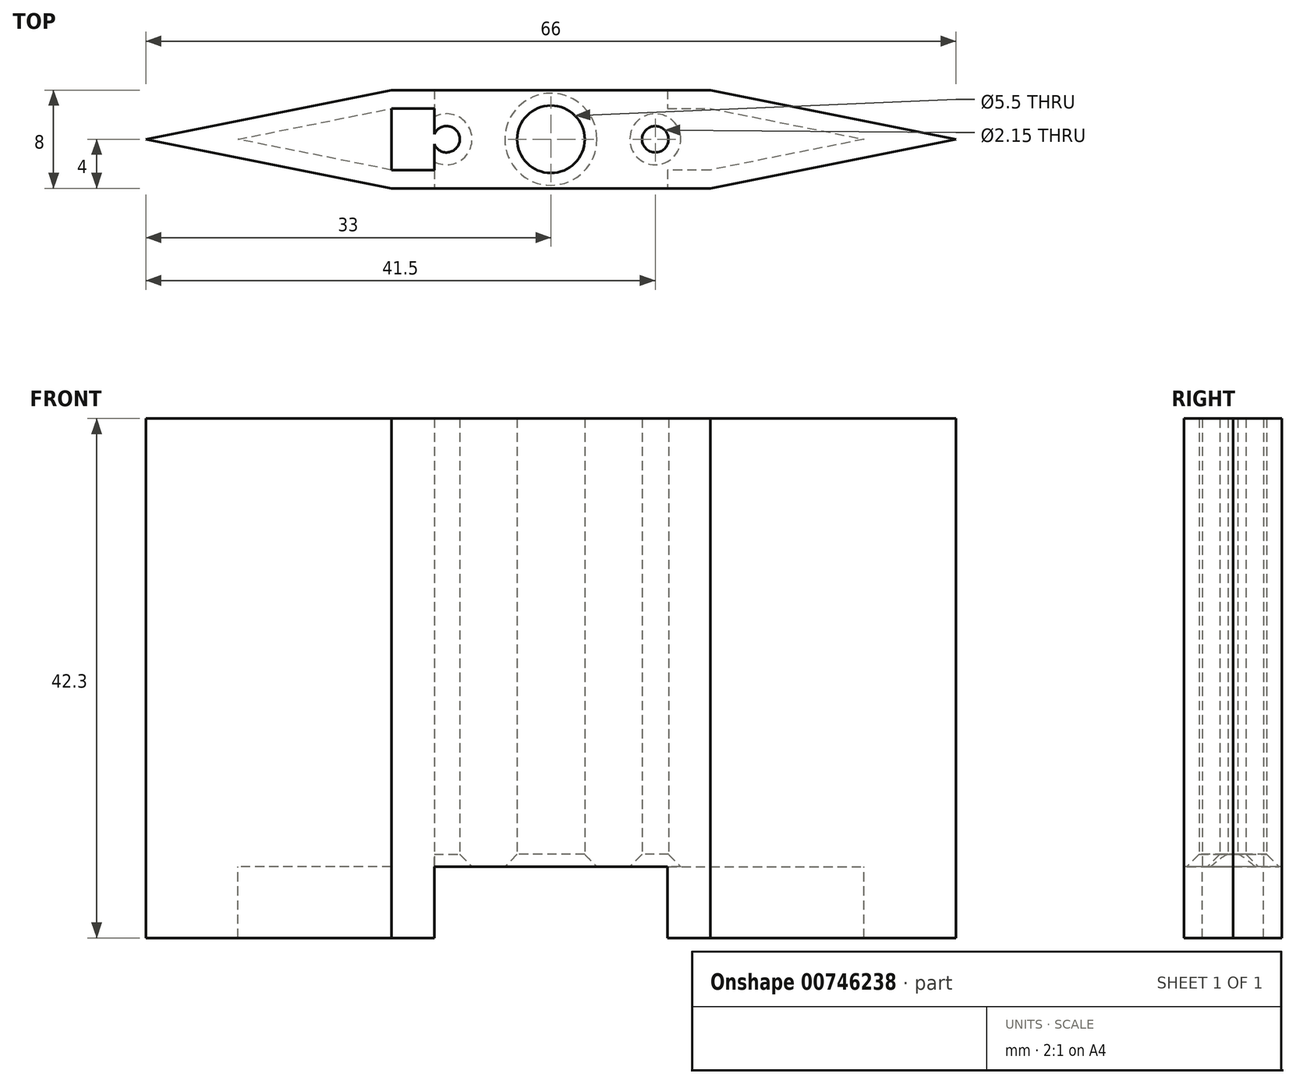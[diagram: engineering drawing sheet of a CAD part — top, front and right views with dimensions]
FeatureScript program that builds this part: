
annotation { "Feature Type Name" : "Feature", "Feature Type Description" : "" }
export const myFeature = defineFeature(function(context is Context, id is Id, definition is map)
    precondition{}
    {
        {
            var Q0;
            Q0=qCreatedBy(makeId("Top.planeOp"),FACE);
            var sketch = newSketch(context, id + "F0", { "sketchPlane" : qUnion([Q0])});
            skCircle(sketch, "E0", {"center": v(-8.5, 0) * mm, "radius": 1.07 * mm});
            skCircle(sketch, "E1", {"center": v(8.5, 0) * mm, "radius": 1.07 * mm});
            skLineSegment(sketch, "E2", {"start": v(-8.5, 0) * mm, "end": v(8.5, 0) * mm});
            skPoint(sketch, "E3", {"position": v(0, 0) * mm});
            skLineSegment(sketch, "E4", {"start": v(-33, 0) * mm, "end": v(-13, 4) * mm});
            skLineSegment(sketch, "E5", {"start": v(-13, 4) * mm, "end": v(13, 4) * mm});
            skLineSegment(sketch, "E6", {"start": v(13, 4) * mm, "end": v(33, 0) * mm});
            skLineSegment(sketch, "E7", {"start": v(33, 0) * mm, "end": v(13, -4) * mm});
            skLineSegment(sketch, "E8", {"start": v(13, -4) * mm, "end": v(-13, -4) * mm});
            skLineSegment(sketch, "E9", {"start": v(-13, -4) * mm, "end": v(-33, 0) * mm});
            skLineSegment(sketch, "E10", {"start": v(-13, 4) * mm, "end": v(-13, -4) * mm});
            skLineSegment(sketch, "E11", {"start": v(13, 4) * mm, "end": v(13, -4) * mm});
            skPoint(sketch, "E12", {"position": v(0, 4) * mm});
            skPoint(sketch, "E13", {"position": v(-13, 0) * mm});
            skLineSegment(sketch, "E14", {"start": v(-33, 0) * mm, "end": v(-13, 0) * mm});
            skLineSegment(sketch, "E15", {"start": v(13, 0) * mm, "end": v(33, 0) * mm});
            skCircle(sketch, "E16", {"center": v(0, 0) * mm, "radius": 2.75 * mm});
            skLineSegment(sketch, "E17", {"start": v(-13, 2.5) * mm, "end": v(13, 2.5) * mm});
            skLineSegment(sketch, "E18", {"start": v(13, 2.5) * mm, "end": v(25.5, 0) * mm});
            skLineSegment(sketch, "E19", {"start": v(25.5, 0) * mm, "end": v(13, -2.5) * mm});
            skLineSegment(sketch, "E20", {"start": v(13, -2.5) * mm, "end": v(-13, -2.5) * mm});
            skLineSegment(sketch, "E21", {"start": v(-13, -2.5) * mm, "end": v(-25.5, 0) * mm});
            skLineSegment(sketch, "E22", {"start": v(-25.5, 0) * mm, "end": v(-13, 2.5) * mm});
            skLineSegment(sketch, "E23", {"start": v(-9.5, 4) * mm, "end": v(-9.5, -4) * mm});
            skLineSegment(sketch, "E24", {"start": v(9.5, 4) * mm, "end": v(9.5, -4) * mm});
            skPoint(sketch, "E25", {"position": v(0, 12.17) * mm});
            skSolve(sketch);
        }
        {
            var Q0;
            Q0=makeQuery(id+"F0.imprint","IMPRINT",FACE,{"disambiguationData":[TD([[makeQuery(id+"F0.imprint","IMPRINT",EDGE,{"derivedFrom":sQuery(id+"F0.wireOp",EDGE,"E0")}),-1.0]])]});
            var Q1;
            {var subQ0=sQuery(id+"F0.wireOp",EDGE,"E9");Q1=makeQuery(id+"F0.imprint","IMPRINT",FACE,{"disambiguationData":[TD([[makeQuery(id+"F0.imprint","IMPRINT",EDGE,{"derivedFrom":subQ0}),-1.0]])]});}
            var Q2;
            {var subQ0=sQuery(id+"F0.wireOp",EDGE,"E4");Q2=makeQuery(id+"F0.imprint","IMPRINT",FACE,{"disambiguationData":[TD([[makeQuery(id+"F0.imprint","IMPRINT",EDGE,{"derivedFrom":subQ0}),-1.0]])]});}
            var Q3;
            {var subQ0=sQuery(id+"F0.wireOp",EDGE,"E7");Q3=makeQuery(id+"F0.imprint","IMPRINT",FACE,{"disambiguationData":[TD([[makeQuery(id+"F0.imprint","IMPRINT",EDGE,{"derivedFrom":subQ0}),-1.0]])]});}
            var Q4;
            {var subQ0=sQuery(id+"F0.wireOp",EDGE,"E6");Q4=makeQuery(id+"F0.imprint","IMPRINT",FACE,{"disambiguationData":[TD([[makeQuery(id+"F0.imprint","IMPRINT",EDGE,{"derivedFrom":subQ0}),-1.0]])]});}
            var Q5;
            {var subQ3=sQuery(id+"F0.wireOp",EDGE,"E21");Q5=makeQuery(id+"F0.imprint","IMPRINT",FACE,{"disambiguationData":[TD([[makeQuery(id+"F0.imprint","IMPRINT",EDGE,{"derivedFrom":subQ3}),-1.0]])]});}
            var Q6;
            {var subQ3=sQuery(id+"F0.wireOp",EDGE,"E22");Q6=makeQuery(id+"F0.imprint","IMPRINT",FACE,{"disambiguationData":[TD([[makeQuery(id+"F0.imprint","IMPRINT",EDGE,{"derivedFrom":subQ3}),-1.0]])]});}
            var Q7;
            {var subQ0=sQuery(id+"F0.wireOp",EDGE,"E5");Q7=makeQuery(id+"F0.imprint","IMPRINT",FACE,{"disambiguationData":[TD([[makeQuery(id+"F0.imprint","IMPRINT",EDGE,{"derivedFrom":subQ0}),-1.0]])]});}
            var Q8;
            {var subQ0=sQuery(id+"F0.wireOp",EDGE,"E8");Q8=makeQuery(id+"F0.imprint","IMPRINT",FACE,{"disambiguationData":[TD([[makeQuery(id+"F0.imprint","IMPRINT",EDGE,{"derivedFrom":subQ0}),-1.0]])]});}
            var Q9;
            {var subQ3=sQuery(id+"F0.wireOp",EDGE,"E19");Q9=makeQuery(id+"F0.imprint","IMPRINT",FACE,{"disambiguationData":[TD([[makeQuery(id+"F0.imprint","IMPRINT",EDGE,{"derivedFrom":subQ3}),-1.0]])]});}
            var Q10;
            {var subQ3=sQuery(id+"F0.wireOp",EDGE,"E18");Q10=makeQuery(id+"F0.imprint","IMPRINT",FACE,{"disambiguationData":[TD([[makeQuery(id+"F0.imprint","IMPRINT",EDGE,{"derivedFrom":subQ3}),-1.0]])]});}
            var Q11;
            {var subQ3=sQuery(id+"F0.wireOp",EDGE,"E24");var subQ5=sQuery(id+"F0.wireOp",EDGE,"E17");var subQ7=makeQuery(id+"F0.imprint","INTERSECT",VERTEX,{"derivedFrom":[subQ5,subQ3]});Q11=makeQuery(id+"F0.imprint","IMPRINT",FACE,{"disambiguationData":[TD([[makeQuery(id+"F0.imprint","IMPRINT",EDGE,{"disambiguationData":[TD([[subQ7,-1.0]])],"derivedFrom":subQ3}),1.0]])]});}
            var Q12;
            Q12=makeQuery(id+"F0.imprint","IMPRINT",FACE,{"disambiguationData":[TD([[makeQuery(id+"F0.imprint","IMPRINT",EDGE,{"derivedFrom":sQuery(id+"F0.wireOp",EDGE,"E1")}),-1.0]])]});
            var Q13;
            {var subQ0=sQuery(id+"F0.wireOp",EDGE,"E23");var subQ1=sQuery(id+"F0.wireOp",EDGE,"E5");var subQ2=makeQuery(id+"F0.imprint","INTERSECT",VERTEX,{"derivedFrom":[subQ1,subQ0]});Q13=makeQuery(id+"F0.imprint","IMPRINT",FACE,{"disambiguationData":[TD([[makeQuery(id+"F0.imprint","IMPRINT",EDGE,{"disambiguationData":[TD([[subQ2,-1.0]])],"derivedFrom":subQ1}),-1.0]])]});}
            var Q14;
            {var subQ0=sQuery(id+"F0.wireOp",EDGE,"E23");var subQ1=sQuery(id+"F0.wireOp",EDGE,"E8");var subQ2=makeQuery(id+"F0.imprint","INTERSECT",VERTEX,{"derivedFrom":[subQ1,subQ0]});Q14=makeQuery(id+"F0.imprint","IMPRINT",FACE,{"disambiguationData":[TD([[makeQuery(id+"F0.imprint","IMPRINT",EDGE,{"disambiguationData":[TD([[subQ2,1.0]])],"derivedFrom":subQ1}),-1.0]])]});}
            var Q15;
            {var subQ3=sQuery(id+"F0.wireOp",EDGE,"E23");var subQ9=sQuery(id+"F0.wireOp",EDGE,"E0");var subQ11=makeQuery(id+"F0.imprint","INTERSECT",VERTEX,{"disambiguationData":[OD(0.0)],"derivedFrom":[subQ9,subQ3]});Q15=makeQuery(id+"F0.imprint","IMPRINT",FACE,{"disambiguationData":[TD([[makeQuery(id+"F0.imprint","IMPRINT",EDGE,{"disambiguationData":[TD([[subQ11,-1.0]])],"derivedFrom":subQ9}),-1.0]])]});}
            extrude(context, id + "F1", {"entities" : qUnion([Q0, Q1, Q2, Q3, Q4, Q5, Q6, Q7, Q8, Q9, Q10, Q11, Q12, Q13, Q14, Q15]), "depth" : 35 * mm, "offsetDistance" : 25 * mm});
        }
        {
            var Q0;
            {var subQ0=sQuery(id+"F0.wireOp",EDGE,"E9");Q0=makeQuery(id+"F0.imprint","IMPRINT",FACE,{"disambiguationData":[TD([[makeQuery(id+"F0.imprint","IMPRINT",EDGE,{"derivedFrom":subQ0}),-1.0]])]});}
            var Q1;
            {var subQ0=sQuery(id+"F0.wireOp",EDGE,"E4");Q1=makeQuery(id+"F0.imprint","IMPRINT",FACE,{"disambiguationData":[TD([[makeQuery(id+"F0.imprint","IMPRINT",EDGE,{"derivedFrom":subQ0}),-1.0]])]});}
            var Q2;
            {var subQ0=sQuery(id+"F0.wireOp",EDGE,"E5");Q2=makeQuery(id+"F0.imprint","IMPRINT",FACE,{"disambiguationData":[TD([[makeQuery(id+"F0.imprint","IMPRINT",EDGE,{"derivedFrom":subQ0}),-1.0]])]});}
            var Q3;
            {var subQ3=sQuery(id+"F0.wireOp",EDGE,"E22");Q3=makeQuery(id+"F0.imprint","IMPRINT",FACE,{"disambiguationData":[TD([[makeQuery(id+"F0.imprint","IMPRINT",EDGE,{"derivedFrom":subQ3}),-1.0]])]});}
            var Q4;
            {var subQ3=sQuery(id+"F0.wireOp",EDGE,"E21");Q4=makeQuery(id+"F0.imprint","IMPRINT",FACE,{"disambiguationData":[TD([[makeQuery(id+"F0.imprint","IMPRINT",EDGE,{"derivedFrom":subQ3}),-1.0]])]});}
            var Q5;
            Q5=makeQuery(id+"F0.imprint","IMPRINT",FACE,{"disambiguationData":[TD([[makeQuery(id+"F0.imprint","IMPRINT",EDGE,{"derivedFrom":sQuery(id+"F0.wireOp",EDGE,"E0")}),-1.0]])]});
            var Q6;
            {var subQ0=sQuery(id+"F0.wireOp",EDGE,"E8");Q6=makeQuery(id+"F0.imprint","IMPRINT",FACE,{"disambiguationData":[TD([[makeQuery(id+"F0.imprint","IMPRINT",EDGE,{"derivedFrom":subQ0}),-1.0]])]});}
            var Q7;
            {var subQ0=sQuery(id+"F0.wireOp",EDGE,"E7");Q7=makeQuery(id+"F0.imprint","IMPRINT",FACE,{"disambiguationData":[TD([[makeQuery(id+"F0.imprint","IMPRINT",EDGE,{"derivedFrom":subQ0}),-1.0]])]});}
            var Q8;
            {var subQ3=sQuery(id+"F0.wireOp",EDGE,"E19");Q8=makeQuery(id+"F0.imprint","IMPRINT",FACE,{"disambiguationData":[TD([[makeQuery(id+"F0.imprint","IMPRINT",EDGE,{"derivedFrom":subQ3}),-1.0]])]});}
            var Q9;
            {var subQ3=sQuery(id+"F0.wireOp",EDGE,"E18");Q9=makeQuery(id+"F0.imprint","IMPRINT",FACE,{"disambiguationData":[TD([[makeQuery(id+"F0.imprint","IMPRINT",EDGE,{"derivedFrom":subQ3}),-1.0]])]});}
            var Q10;
            {var subQ0=sQuery(id+"F0.wireOp",EDGE,"E6");Q10=makeQuery(id+"F0.imprint","IMPRINT",FACE,{"disambiguationData":[TD([[makeQuery(id+"F0.imprint","IMPRINT",EDGE,{"derivedFrom":subQ0}),-1.0]])]});}
            var Q11;
            Q11=makeQuery(id+"F0.imprint","IMPRINT",FACE,{"disambiguationData":[TD([[makeQuery(id+"F0.imprint","IMPRINT",EDGE,{"derivedFrom":sQuery(id+"F0.wireOp",EDGE,"E1")}),-1.0]])]});
            var Q12;
            {var subQ3=sQuery(id+"F0.wireOp",EDGE,"E24");var subQ5=sQuery(id+"F0.wireOp",EDGE,"E17");var subQ7=makeQuery(id+"F0.imprint","INTERSECT",VERTEX,{"derivedFrom":[subQ5,subQ3]});Q12=makeQuery(id+"F0.imprint","IMPRINT",FACE,{"disambiguationData":[TD([[makeQuery(id+"F0.imprint","IMPRINT",EDGE,{"disambiguationData":[TD([[subQ7,-1.0]])],"derivedFrom":subQ3}),1.0]])]});}
            var Q13;
            {var subQ0=sQuery(id+"F0.wireOp",EDGE,"E23");var subQ1=sQuery(id+"F0.wireOp",EDGE,"E8");var subQ2=makeQuery(id+"F0.imprint","INTERSECT",VERTEX,{"derivedFrom":[subQ1,subQ0]});Q13=makeQuery(id+"F0.imprint","IMPRINT",FACE,{"disambiguationData":[TD([[makeQuery(id+"F0.imprint","IMPRINT",EDGE,{"disambiguationData":[TD([[subQ2,1.0]])],"derivedFrom":subQ1}),-1.0]])]});}
            var Q14;
            {var subQ0=sQuery(id+"F0.wireOp",EDGE,"E23");var subQ1=sQuery(id+"F0.wireOp",EDGE,"E5");var subQ2=makeQuery(id+"F0.imprint","INTERSECT",VERTEX,{"derivedFrom":[subQ1,subQ0]});Q14=makeQuery(id+"F0.imprint","IMPRINT",FACE,{"disambiguationData":[TD([[makeQuery(id+"F0.imprint","IMPRINT",EDGE,{"disambiguationData":[TD([[subQ2,-1.0]])],"derivedFrom":subQ1}),-1.0]])]});}
            var Q15;
            {var subQ3=sQuery(id+"F0.wireOp",EDGE,"E23");var subQ9=sQuery(id+"F0.wireOp",EDGE,"E0");var subQ11=makeQuery(id+"F0.imprint","INTERSECT",VERTEX,{"disambiguationData":[OD(0.0)],"derivedFrom":[subQ9,subQ3]});Q15=makeQuery(id+"F0.imprint","IMPRINT",FACE,{"disambiguationData":[TD([[makeQuery(id+"F0.imprint","IMPRINT",EDGE,{"disambiguationData":[TD([[subQ11,-1.0]])],"derivedFrom":subQ9}),-1.0]])]});}
            extrude(context, id + "F2", {"entities" : qUnion([Q0, Q1, Q2, Q3, Q4, Q5, Q6, Q7, Q8, Q9, Q10, Q11, Q12, Q13, Q14, Q15]), "operationType" : NewBodyOperationType.ADD, "oppositeDirection" : true, "depth" : 1.5 * mm, "offsetDistance" : 25 * mm});
        }
        {
            var Q0;
            Q0=makeQuery(id+"F4.opExtrude","SWEPT_EDGE",EDGE,{"disambiguationData":[OSD([sQuery(id+"F0.wireOp",EDGE,"E20"),sQuery(id+"F0.wireOp",EDGE,"E23")])]});
            var Q1;
            Q1=makeQuery(id+"F4.opExtrude","SWEPT_EDGE",EDGE,{"disambiguationData":[OSD([sQuery(id+"F0.wireOp",EDGE,"E17"),sQuery(id+"F0.wireOp",EDGE,"E23")])]});
            var Q2;
            Q2=makeQuery(id+"F4.opExtrude","SWEPT_EDGE",EDGE,{"disambiguationData":[OSD([sQuery(id+"F0.wireOp",EDGE,"E20"),sQuery(id+"F0.wireOp",EDGE,"E24")])]});
            var Q3;
            Q3=makeQuery(id+"F4.opExtrude","SWEPT_EDGE",EDGE,{"disambiguationData":[OSD([sQuery(id+"F0.wireOp",EDGE,"E17"),sQuery(id+"F0.wireOp",EDGE,"E24")])]});
            var Q4;
            {var subQ0=sQuery(id+"F0.wireOp",EDGE,"E0");Q4=makeQuery(id+"F2.opExtrude","CAP_EDGE",EDGE,{"disambiguationData":[OSD([subQ0]),TDD([makeQuery(id+"F0.imprint","IMPRINT",EDGE,{"derivedFrom":subQ0})])],"isStart":false});}
            var Q5;
            {var subQ0=sQuery(id+"F0.wireOp",EDGE,"E24");var subQ1=sQuery(id+"F0.wireOp",EDGE,"E1");var subQ2=makeQuery(id+"F0.imprint","INTERSECT",VERTEX,{"disambiguationData":[OD(0.0)],"derivedFrom":[subQ1,subQ0]});var subQ4=makeQuery(id+"F0.imprint","INTERSECT",VERTEX,{"derivedFrom":[subQ1,sQuery(id+"F0.wireOp",EDGE,"E2")]});Q5=makeQuery(id+"F2.opExtrude","CAP_EDGE",EDGE,{"disambiguationData":[OSD([subQ1]),TDD([makeQuery(id+"F0.imprint","IMPRINT",EDGE,{"disambiguationData":[TD([[subQ4,1.0]])],"derivedFrom":subQ1}),makeQuery(id+"F0.imprint","IMPRINT",EDGE,{"disambiguationData":[TD([[subQ4,-1.0]])],"derivedFrom":subQ1}),makeQuery(id+"F0.imprint","IMPRINT",EDGE,{"disambiguationData":[TD([[subQ2,1.0]])],"derivedFrom":subQ1})])],"isStart":false});}
            var Q6;
            {var subQ0=sQuery(id+"F0.wireOp",EDGE,"E16");var subQ1=sQuery(id+"F0.wireOp",EDGE,"E2");var subQ2=makeQuery(id+"F0.imprint","INTERSECT",VERTEX,{"disambiguationData":[OD(1.0)],"derivedFrom":[subQ1,subQ0]});var subQ4=makeQuery(id+"F0.imprint","INTERSECT",VERTEX,{"disambiguationData":[OD(0.0)],"derivedFrom":[subQ1,subQ0]});Q6=makeQuery(id+"F2.opExtrude","CAP_EDGE",EDGE,{"disambiguationData":[OSD([subQ0]),TDD([makeQuery(id+"F0.imprint","IMPRINT",EDGE,{"disambiguationData":[TD([[subQ2,-1.0]])],"derivedFrom":subQ0}),makeQuery(id+"F0.imprint","IMPRINT",EDGE,{"disambiguationData":[TD([[subQ4,1.0]])],"derivedFrom":subQ0}),makeQuery(id+"F0.imprint","IMPRINT",EDGE,{"disambiguationData":[TD([[subQ4,-1.0]])],"derivedFrom":subQ0}),makeQuery(id+"F0.imprint","IMPRINT",EDGE,{"disambiguationData":[TD([[subQ2,1.0]])],"derivedFrom":subQ0})])],"isStart":false});}
            chamfer(context, id + "F3", {"entities" : qUnion([Q0, Q1, Q2, Q3, Q4, Q5, Q6]), "width" : 1 * mm, "tangentPropagation" : true});
        }
        {
            var Q0;
            {var subQ1=sQuery(id+"F0.wireOp",EDGE,"E5");var subQ3=sQuery(id+"F0.wireOp",EDGE,"E23");var subQ4=makeQuery(id+"F0.imprint","INTERSECT",VERTEX,{"derivedFrom":[subQ1,subQ3]});Q0=makeQuery(id+"F0.imprint","IMPRINT",FACE,{"disambiguationData":[TD([[makeQuery(id+"F0.imprint","IMPRINT",EDGE,{"disambiguationData":[TD([[subQ4,-1.0]])],"derivedFrom":subQ3}),-1.0]])]});}
            var Q1;
            {var subQ1=sQuery(id+"F0.wireOp",EDGE,"E5");var subQ3=sQuery(id+"F0.wireOp",EDGE,"E24");var subQ4=makeQuery(id+"F0.imprint","INTERSECT",VERTEX,{"derivedFrom":[subQ1,subQ3]});Q1=makeQuery(id+"F0.imprint","IMPRINT",FACE,{"disambiguationData":[TD([[makeQuery(id+"F0.imprint","IMPRINT",EDGE,{"disambiguationData":[TD([[subQ4,-1.0]])],"derivedFrom":subQ3}),1.0]])]});}
            var Q2;
            {var subQ0=sQuery(id+"F0.wireOp",EDGE,"E4");Q2=makeQuery(id+"F0.imprint","IMPRINT",FACE,{"disambiguationData":[TD([[makeQuery(id+"F0.imprint","IMPRINT",EDGE,{"derivedFrom":subQ0}),-1.0]])]});}
            var Q3;
            {var subQ0=sQuery(id+"F0.wireOp",EDGE,"E9");Q3=makeQuery(id+"F0.imprint","IMPRINT",FACE,{"disambiguationData":[TD([[makeQuery(id+"F0.imprint","IMPRINT",EDGE,{"derivedFrom":subQ0}),-1.0]])]});}
            var Q4;
            {var subQ1=sQuery(id+"F0.wireOp",EDGE,"E8");var subQ3=sQuery(id+"F0.wireOp",EDGE,"E24");var subQ4=makeQuery(id+"F0.imprint","INTERSECT",VERTEX,{"derivedFrom":[subQ1,subQ3]});Q4=makeQuery(id+"F0.imprint","IMPRINT",FACE,{"disambiguationData":[TD([[makeQuery(id+"F0.imprint","IMPRINT",EDGE,{"disambiguationData":[TD([[subQ4,1.0]])],"derivedFrom":subQ3}),1.0]])]});}
            var Q5;
            {var subQ1=sQuery(id+"F0.wireOp",EDGE,"E8");var subQ3=sQuery(id+"F0.wireOp",EDGE,"E23");var subQ4=makeQuery(id+"F0.imprint","INTERSECT",VERTEX,{"derivedFrom":[subQ1,subQ3]});Q5=makeQuery(id+"F0.imprint","IMPRINT",FACE,{"disambiguationData":[TD([[makeQuery(id+"F0.imprint","IMPRINT",EDGE,{"disambiguationData":[TD([[subQ4,1.0]])],"derivedFrom":subQ3}),-1.0]])]});}
            var Q6;
            {var subQ0=sQuery(id+"F0.wireOp",EDGE,"E6");Q6=makeQuery(id+"F0.imprint","IMPRINT",FACE,{"disambiguationData":[TD([[makeQuery(id+"F0.imprint","IMPRINT",EDGE,{"derivedFrom":subQ0}),-1.0]])]});}
            var Q7;
            {var subQ0=sQuery(id+"F0.wireOp",EDGE,"E7");Q7=makeQuery(id+"F0.imprint","IMPRINT",FACE,{"disambiguationData":[TD([[makeQuery(id+"F0.imprint","IMPRINT",EDGE,{"derivedFrom":subQ0}),-1.0]])]});}
            extrude(context, id + "F4", {"entities" : qUnion([Q0, Q1, Q2, Q3, Q4, Q5, Q6, Q7]), "operationType" : NewBodyOperationType.ADD, "oppositeDirection" : true, "depth" : 7.3 * mm, "offsetDistance" : 25 * mm});
        }
    });
